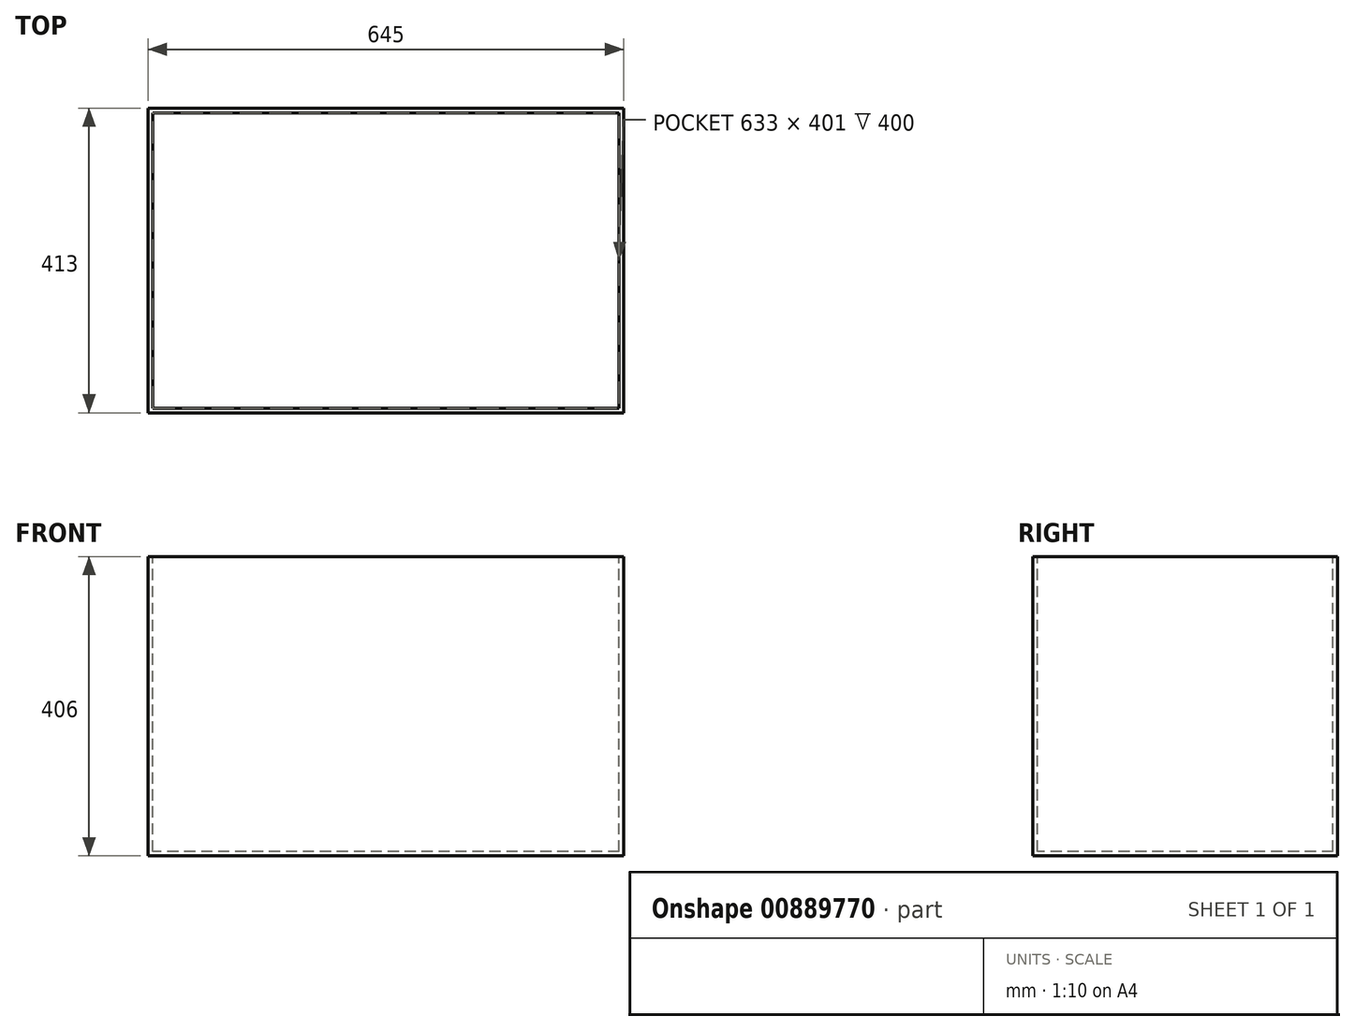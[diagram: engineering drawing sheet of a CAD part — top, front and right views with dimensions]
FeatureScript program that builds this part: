
annotation { "Feature Type Name" : "Feature", "Feature Type Description" : "" }
export const myFeature = defineFeature(function(context is Context, id is Id, definition is map)
    precondition{}
    {
        {
            var Q0;
            Q0=qCreatedBy(makeId("Top.planeOp"),FACE);
            var sketch = newSketch(context, id + "F0", { "sketchPlane" : qUnion([Q0])});
            skLineSegment(sketch, "E0.bottom", {"start": v(322.5, 206.5) * mm, "end": v(-322.5, 206.5) * mm});
            skLineSegment(sketch, "E0.top", {"start": v(322.5, -206.5) * mm, "end": v(-322.5, -206.5) * mm});
            skLineSegment(sketch, "E0.left", {"start": v(322.5, 206.5) * mm, "end": v(322.5, -206.5) * mm});
            skLineSegment(sketch, "E0.right", {"start": v(-322.5, 206.5) * mm, "end": v(-322.5, -206.5) * mm});
            skPoint(sketch, "E0.middle", {"position": v(0, 0) * mm});
            skLineSegment(sketch, "E1.0", {"start": v(316.5, 200.5) * mm, "end": v(-316.5, 200.5) * mm});
            skLineSegment(sketch, "E1.1", {"start": v(316.5, 200.5) * mm, "end": v(316.5, -200.5) * mm});
            skLineSegment(sketch, "E1.2", {"start": v(316.5, -200.5) * mm, "end": v(-316.5, -200.5) * mm});
            skLineSegment(sketch, "E1.3", {"start": v(-316.5, 200.5) * mm, "end": v(-316.5, -200.5) * mm});
            skSolve(sketch);
        }
        {
            var Q0;
            Q0 = qSketchRegion(id + "F0", true);
            extrude(context, id + "F1", {"entities" : qUnion([Q0]), "oppositeDirection" : true, "depth" : 400 * mm, "offsetDistance" : 25 * mm});
        }
        {
            var Q0;
            Q0=makeQuery(id+"F1.opExtrude","CAP_FACE",FACE,{"disambiguationData":[OSD([sQuery(id+"F0.wireOp",EDGE,"E0.bottom"),sQuery(id+"F0.wireOp",EDGE,"E0.top"),sQuery(id+"F0.wireOp",EDGE,"E0.left"),sQuery(id+"F0.wireOp",EDGE,"E0.right"),sQuery(id+"F0.wireOp",EDGE,"E1.0"),sQuery(id+"F0.wireOp",EDGE,"E1.1"),sQuery(id+"F0.wireOp",EDGE,"E1.2"),sQuery(id+"F0.wireOp",EDGE,"E1.3")])],"isStart":false});
            var sketch = newSketch(context, id + "F2", { "sketchPlane" : qUnion([Q0])});
            skLineSegment(sketch, "E2.0", {"start": v(322.5, 206.5) * mm, "end": v(-322.5, 206.5) * mm});
            skLineSegment(sketch, "E2.1", {"start": v(322.5, -206.5) * mm, "end": v(322.5, 206.5) * mm});
            skLineSegment(sketch, "E2.2", {"start": v(322.5, -206.5) * mm, "end": v(-322.5, -206.5) * mm});
            skLineSegment(sketch, "E2.3", {"start": v(-322.5, -206.5) * mm, "end": v(-322.5, 206.5) * mm});
            skSolve(sketch);
        }
        {
            var Q0;
            Q0 = qSketchRegion(id + "F2", true);
            extrude(context, id + "F3", {"entities" : qUnion([Q0]), "operationType" : NewBodyOperationType.ADD, "depth" : 6 * mm, "offsetDistance" : 25 * mm});
        }
    });
